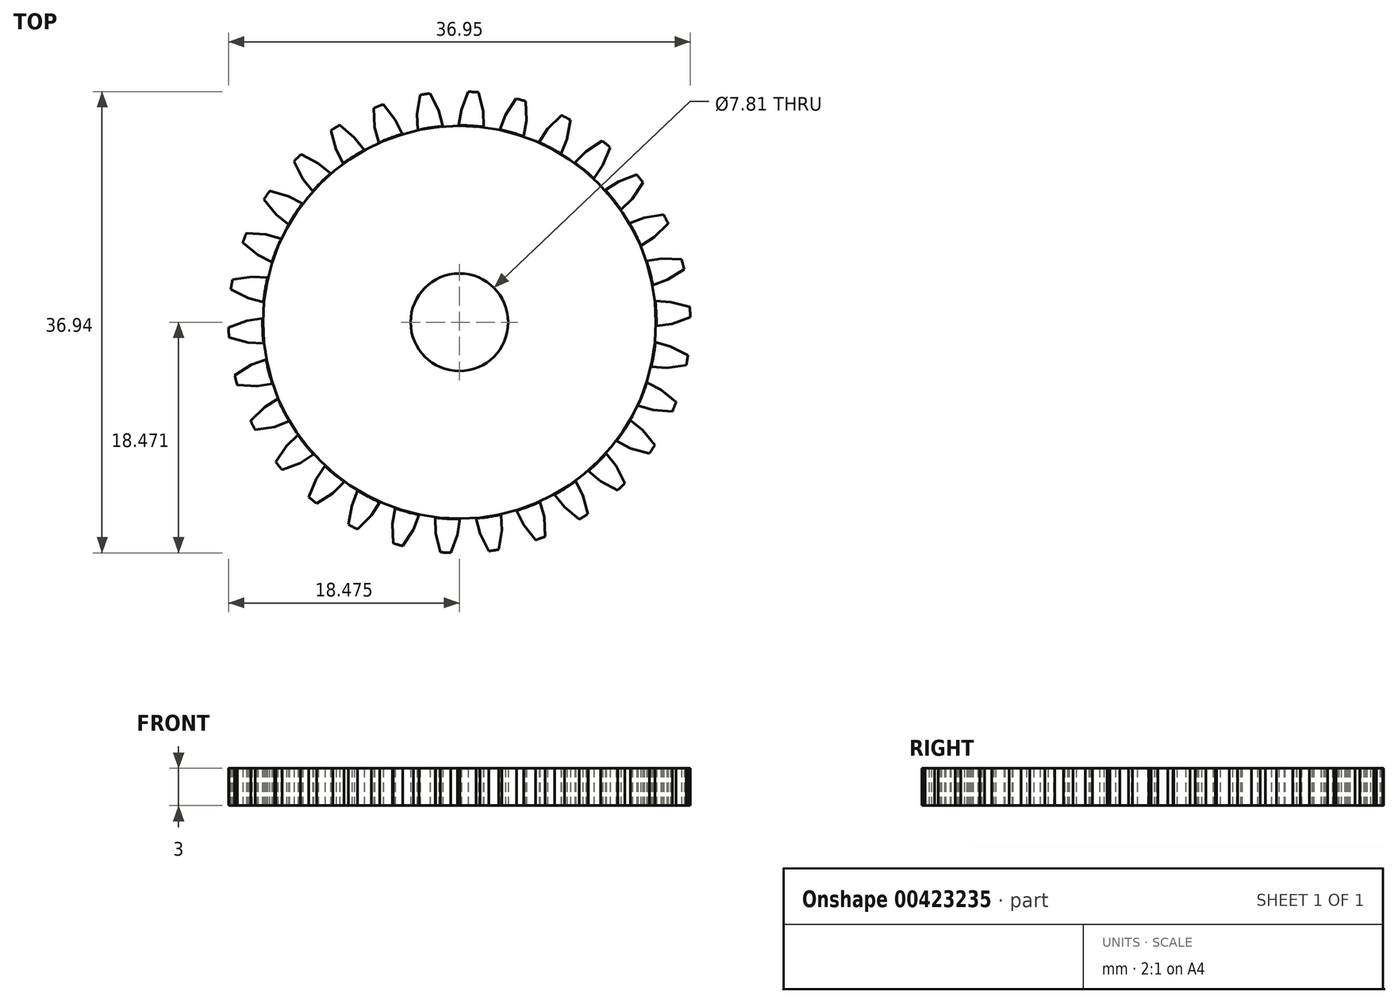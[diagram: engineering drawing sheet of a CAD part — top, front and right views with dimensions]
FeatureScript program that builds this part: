
annotation { "Feature Type Name" : "Feature", "Feature Type Description" : "" }
export const myFeature = defineFeature(function(context is Context, id is Id, definition is map)
    precondition{}
    {
        {
            var Q0;
            Q0=qCreatedBy(makeId("Top.planeOp"),FACE);
            var sketch = newSketch(context, id + "F0", { "sketchPlane" : qUnion([Q0])});
            skLineSegment(sketch, "E0", {"start": v(2.7, 43.64) * mm, "end": v(12.7, 43.64) * mm});
            skSolve(sketch);
        }
        {
            var Q0;
            Q0=qCreatedBy(makeId("Top.planeOp"),FACE);
            var sketch = newSketch(context, id + "F1", { "sketchPlane" : qUnion([Q0])});
            skLineSegment(sketch, "E1.0", {"start": v(2.7, 43.64) * mm, "end": v(12.7, 43.64) * mm});
            skLineSegment(sketch, "E2.top", {"start": v(2.7, -76.36) * mm, "end": v(12.7, -76.36) * mm});
            skLineSegment(sketch, "E2.left", {"start": v(2.7, 43.64) * mm, "end": v(2.7, -76.36) * mm});
            skLineSegment(sketch, "E2.right", {"start": v(12.7, 43.64) * mm, "end": v(12.7, -76.36) * mm});
            skLineSegment(sketch, "E3", {"start": v(2.7, 25.61) * mm, "end": v(12.7, 25.61) * mm, "construction": true});
            skLineSegment(sketch, "E4", {"start": v(-0.54, 23.36) * mm, "end": v(2.7, 23.36) * mm, "construction": true});
            skLineSegment(sketch, "E5.trimOffspring", {"start": v(12.7, 23.36) * mm, "end": v(15.96, 23.36) * mm, "construction": true});
            skSolve(sketch);
        }
        {
            var Q0;
            Q0=qCreatedBy(makeId("Top.planeOp"),FACE);
            var sketch = newSketch(context, id + "F2", { "sketchPlane" : qUnion([Q0])});
            skCircle(sketch, "E6", {"center": v(-27.08, -9.47) * mm, "radius": 3.83 * mm, "construction": true});
            skPoint(sketch, "E6.first.point", {"position": v(-30.8, -8.51) * mm});
            skPoint(sketch, "E6.second.point", {"position": v(-24.15, -7) * mm});
            skPoint(sketch, "E6.third.point", {"position": v(-26, -13.15) * mm});
            skPoint(sketch, "E7.0", {"position": v(7.7, 43.64) * mm});
            skLineSegment(sketch, "E8", {"start": v(7.7, -76.2) * mm, "end": v(7.7, 35.56) * mm, "construction": true});
            skLineSegment(sketch, "E9", {"start": v(85.63, -9.47) * mm, "end": v(-27.08, -9.47) * mm, "construction": true});
            skCircle(sketch, "E10.MirrorC", {"center": v(42.47, -9.47) * mm, "radius": 3.83 * mm, "construction": true});
            skCircle(sketch, "E11", {"center": v(-27.08, -9.47) * mm, "radius": 15.77 * mm, "construction": true});
            skCircle(sketch, "E12.MirrorC", {"center": v(42.47, -9.47) * mm, "radius": 15.77 * mm, "construction": true});
            skCircle(sketch, "E13.MirrorC", {"center": v(7.7, -9.47) * mm, "radius": 3.83 * mm, "construction": true});
            skCircle(sketch, "E14.MirrorC", {"center": v(7.7, -9.47) * mm, "radius": 15.77 * mm, "construction": true});
            skSolve(sketch);
        }
        {
            var Q0;
            Q0=qCreatedBy(makeId("Top.planeOp"),FACE);
            var sketch = newSketch(context, id + "F3", { "sketchPlane" : qUnion([Q0])});
            skPoint(sketch, "E15.0", {"position": v(42.47, -9.47) * mm});
            skCircle(sketch, "E16.0", {"center": v(42.47, -9.47) * mm, "radius": 15.77 * mm});
            skCircle(sketch, "E17.0", {"center": v(42.47, -9.47) * mm, "radius": 3.83 * mm});
            skLineSegment(sketch, "E18.0", {"start": v(7.7, -76.2) * mm, "end": v(7.7, 35.56) * mm});
            skLineSegment(sketch, "E19.0", {"start": v(85.63, -9.47) * mm, "end": v(-27.08, -9.47) * mm});
            skCircle(sketch, "E20.0", {"center": v(7.7, -9.47) * mm, "radius": 3.83 * mm});
            skCircle(sketch, "E21.0", {"center": v(-27.08, -9.47) * mm, "radius": 3.83 * mm});
            skCircle(sketch, "E22", {"center": v(42.47, -9.47) * mm, "radius": 15.73 * mm});
            skCircle(sketch, "E23", {"center": v(42.47, -9.47) * mm, "radius": 3.9 * mm});
            skArc(sketch, "E24", {"start": v(38.49, 5.79) * mm, "mid": v(40.14, 6.13) * mm, "end": v(41.82, 6.29) * mm});
            skLineSegment(sketch, "E25", {"start": v(39.15, 5.94) * mm, "end": v(39.08, 7.2) * mm});
            skLineSegment(sketch, "E26", {"start": v(42.47, -9.47) * mm, "end": v(40.14, 6.09) * mm, "construction": true});
            skPoint(sketch, "E26.endSnap0", {"position": v(40.14, 6.13) * mm});
            skLineSegment(sketch, "E27", {"start": v(40.14, 6.09) * mm, "end": v(39.58, 9.82) * mm, "construction": true});
            skLineSegment(sketch, "E28", {"start": v(39.08, 7.2) * mm, "end": v(39.33, 8.74) * mm});
            skLineSegment(sketch, "E29.MirrorCS", {"start": v(40.82, 7.46) * mm, "end": v(40.13, 8.86) * mm});
            skLineSegment(sketch, "E30.MirrorCS", {"start": v(41.13, 6.24) * mm, "end": v(40.82, 7.46) * mm});
            skArc(sketch, "E31.trimOffspring", {"start": v(40.13, 8.86) * mm, "mid": v(39.73, 8.8) * mm, "end": v(39.33, 8.74) * mm});
            skSolve(sketch);
        }
        {
            var Q0;
            {var subQ0=sQuery(id+"F3.wireOp",EDGE,"E22");var subQ1=sQuery(id+"F3.wireOp",EDGE,"E19.0");var subQ2=makeQuery(id+"F3.imprint","INTERSECT",VERTEX,{"disambiguationData":[OD(0.0)],"derivedFrom":[subQ1,subQ0]});Q0=makeQuery(id+"F3.imprint","IMPRINT",FACE,{"disambiguationData":[TD([[makeQuery(id+"F3.imprint","IMPRINT",EDGE,{"disambiguationData":[TD([[subQ2,-1.0]])],"derivedFrom":subQ1}),-1.0]])]});}
            var Q1;
            {var subQ0=sQuery(id+"F3.wireOp",EDGE,"E22");var subQ1=sQuery(id+"F3.wireOp",EDGE,"E19.0");var subQ2=makeQuery(id+"F3.imprint","INTERSECT",VERTEX,{"disambiguationData":[OD(0.0)],"derivedFrom":[subQ1,subQ0]});Q1=makeQuery(id+"F3.imprint","IMPRINT",FACE,{"disambiguationData":[TD([[makeQuery(id+"F3.imprint","IMPRINT",EDGE,{"disambiguationData":[TD([[subQ2,-1.0]])],"derivedFrom":subQ1}),1.0]])]});}
            extrude(context, id + "F4", {"entities" : qUnion([Q0, Q1]), "depth" : 3 * mm});
        }
        {
            var Q0;
            Q0 = qSketchRegion(id + "F2", true);
            var Q1;
            {var subQ0=sQuery(id+"F3.wireOp",EDGE,"E25");Q1=makeQuery(id+"F3.imprint","IMPRINT",FACE,{"disambiguationData":[TD([[makeQuery(id+"F3.imprint","IMPRINT",EDGE,{"derivedFrom":subQ0}),-1.0]])]});}
            var Q2;
            Q2=makeQuery(id+"F4.opExtrude","CAP_FACE",FACE,{"disambiguationData":[OSD([sQuery(id+"F3.wireOp",EDGE,"E22"),sQuery(id+"F3.wireOp",EDGE,"E23")])],"isStart":false});
            extrude(context, id + "F5", {"entities" : qUnion([Q0, Q1]), "operationType" : NewBodyOperationType.ADD, "endBound" : BoundingType.UP_TO_SURFACE, "endBoundEntityFace" : qUnion([Q2]), "depth" : 25 * mm});
        }
        {
            var Q0;
            Q0=makeQuery(id+"F5.opExtrude","SWEPT_BODY",BODY,{"disambiguationData":[OSD([sQuery(id+"F3.wireOp",EDGE,"E16.0"),sQuery(id+"F3.wireOp",EDGE,"E25"),sQuery(id+"F3.wireOp",EDGE,"E28"),sQuery(id+"F3.wireOp",EDGE,"E29.MirrorCS"),sQuery(id+"F3.wireOp",EDGE,"E30.MirrorCS"),sQuery(id+"F3.wireOp",EDGE,"E31.trimOffspring")])]});
            var Q1;
            Q1=sQuery(id+"F3.wireOp",EDGE,"E22");
            circularPattern(context, id + "F6", {"operationType" : NewBodyOperationType.ADD, "entities" : qUnion([Q0]), "axis" : qUnion([Q1]), "angle" : 360 * degree, "instanceCount" : 30, "equalSpace" : true, "isCentered" : true});
        }
    });
